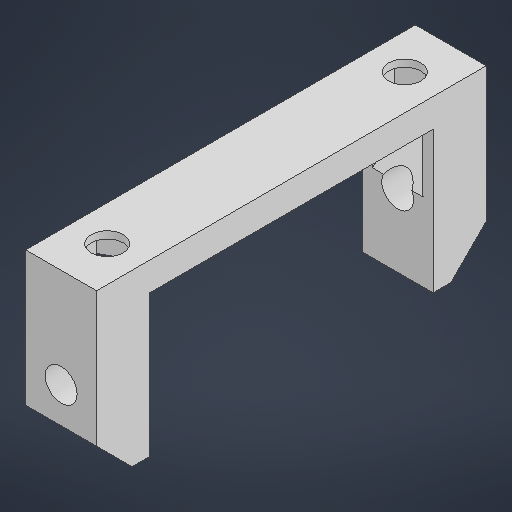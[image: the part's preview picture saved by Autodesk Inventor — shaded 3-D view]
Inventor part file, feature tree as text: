
AUTODESK INVENTOR PART (.ipt)
format: ipt  version: 2025.1 (Build 291241000, 241)  size: 291,328 bytes
history: native  units: mm
features: extrude x5, sketch x3, chamfer x2, projected_geometry x2, plane x1, mirror x1
ambient origin geometry x8: Origin, YZ Plane, XZ Plane, XY Plane, X Axis, Y Axis, Z Axis, Center Point
bodies: Solid1 (feature_tree)
feature tree (14):
  sketch  "Sketch1"  dims[d2=10.0mm d3=55.0mm]
  extrude  "Extrusion1"  Depth=55.0mm
  extrude  "Extrusion2"  Depth=7.1mm
  plane  "Work Plane1"
  extrude  "Extrusion3"  Depth=10.0mm
  extrude  "Extrusion4"  Depth=4.0mm TaperAngle=0.0deg
  chamfer  "Chamfer1"  Distance=3.0mm
  extrude  "Extrusion5"  Depth=20.0mm
  chamfer  "Chamfer2"  Distance=4.5mm
  mirror  "Mirror1"
  sketch  "Sketch2"  dims[d4=7.1mm d5=7.1mm]
  projected_geometry  "Projected Loop1"
  sketch  "Sketch3"  dims[d6=42.0mm d7=4.5mm d8=4.0mm d9=0.0mm d10=3.0mm d11=0.0mm d12=20.0mm d13=4.5mm d15=20.0mm d16=8.0mm d17=8.0mm d18=10.0mm d19=20.0mm d20=20.0mm d21=0.0mm d22=4.0mm d23=0.0mm d24=5.0mm d25=2.0mm d26=45.0deg d27=10.0mm d28=4.5mm d29=0.0mm d30=0.0mm d31=5.0mm d32=2.0mm d33=45.0deg d34=0.872665mm]
  projected_geometry  "Projected Loop2"
